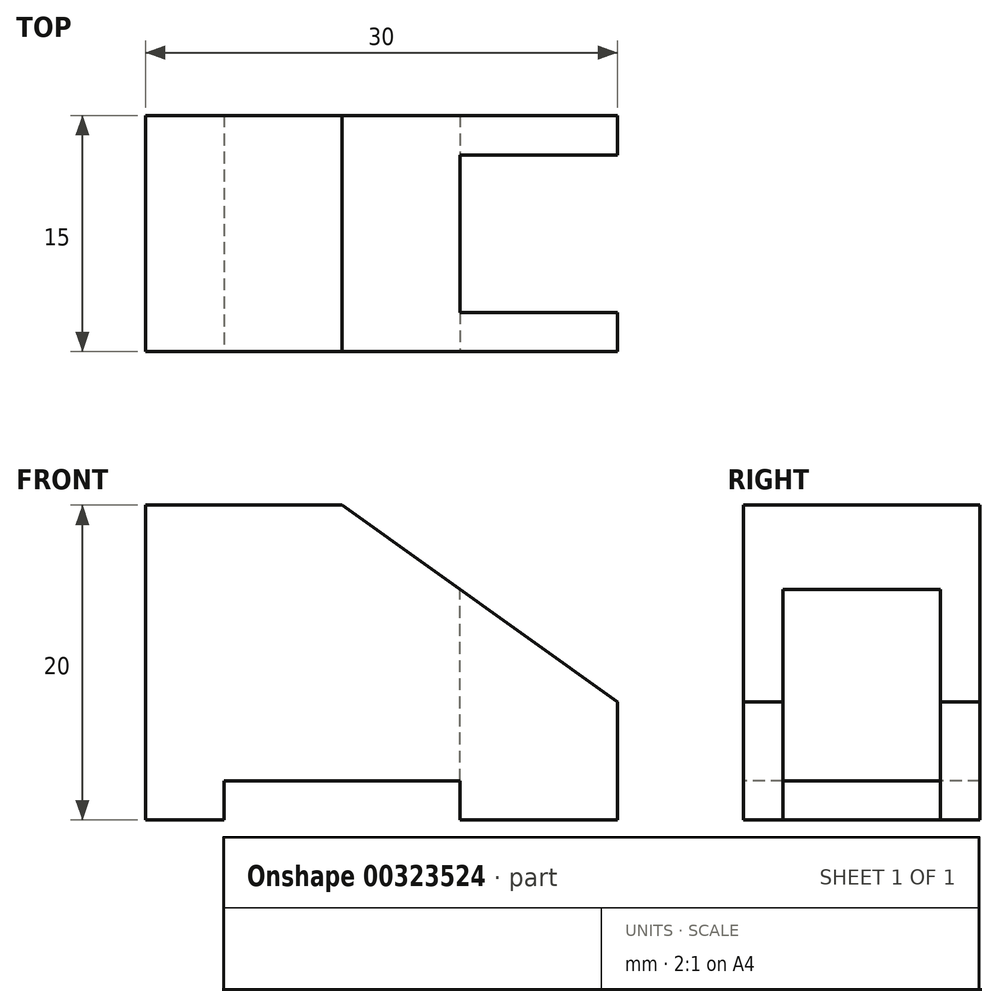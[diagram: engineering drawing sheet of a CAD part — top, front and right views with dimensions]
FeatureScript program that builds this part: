
annotation { "Feature Type Name" : "Feature", "Feature Type Description" : "" }
export const myFeature = defineFeature(function(context is Context, id is Id, definition is map)
    precondition{}
    {
        {
            var Q0;
            Q0=qCreatedBy(makeId("Front.planeOp"),FACE);
            var sketch = newSketch(context, id + "F0", { "sketchPlane" : qUnion([Q0])});
            skLineSegment(sketch, "E0", {"start": v(0, 0) * mm, "end": v(30, 0) * mm});
            skLineSegment(sketch, "E1", {"start": v(30, 0) * mm, "end": v(30, 20) * mm});
            skLineSegment(sketch, "E2", {"start": v(30, 20) * mm, "end": v(0, 20) * mm});
            skLineSegment(sketch, "E3", {"start": v(0, 20) * mm, "end": v(0, 0) * mm});
            skSolve(sketch);
        }
        {
            var Q0;
            Q0=makeQuery(id+"F0.imprint","IMPRINT",FACE,{"disambiguationData":[TD([[makeQuery(id+"F0.imprint","IMPRINT",EDGE,{"derivedFrom":sQuery(id+"F0.wireOp",EDGE,"E0")}),1.0]])]});
            extrude(context, id + "F1", {"entities" : qUnion([Q0]), "oppositeDirection" : true, "depth" : 15 * mm});
        }
        {
            var Q0;
            Q0=makeQuery(id+"F1.opExtrude","CAP_FACE",FACE,{"disambiguationData":[OSD([sQuery(id+"F0.wireOp",EDGE,"E0"),sQuery(id+"F0.wireOp",EDGE,"E1"),sQuery(id+"F0.wireOp",EDGE,"E2"),sQuery(id+"F0.wireOp",EDGE,"E3")])],"isStart":true});
            var sketch = newSketch(context, id + "F2", { "sketchPlane" : qUnion([Q0])});
            skLineSegment(sketch, "E4", {"start": v(0, 0) * mm, "end": v(5, 0) * mm, "construction": true});
            skLineSegment(sketch, "E5", {"start": v(5, 0) * mm, "end": v(5, 2.5) * mm});
            skLineSegment(sketch, "E6", {"start": v(5, 2.5) * mm, "end": v(20, 2.5) * mm});
            skLineSegment(sketch, "E7", {"start": v(20, 2.5) * mm, "end": v(20, 0) * mm});
            skLineSegment(sketch, "E8", {"start": v(20, 0) * mm, "end": v(5, 0) * mm});
            skSolve(sketch);
        }
        {
            var Q0;
            Q0=makeQuery(id+"F2.imprint","IMPRINT",FACE,{"disambiguationData":[TD([[makeQuery(id+"F2.imprint","IMPRINT",EDGE,{"derivedFrom":sQuery(id+"F2.wireOp",EDGE,"E5")}),-1.0]])]});
            extrude(context, id + "F3", {"entities" : qUnion([Q0]), "operationType" : NewBodyOperationType.REMOVE, "oppositeDirection" : true, "depth" : 25 * mm});
        }
        {
            var Q0;
            Q0=makeQuery(id+"F1.opExtrude","SWEPT_FACE",FACE,{"disambiguationData":[OSD([sQuery(id+"F0.wireOp",EDGE,"E2")])]});
            var sketch = newSketch(context, id + "F4", { "sketchPlane" : qUnion([Q0])});
            skLineSegment(sketch, "E9", {"start": v(30, 15) * mm, "end": v(30, 12.5) * mm, "construction": true});
            skLineSegment(sketch, "E10", {"start": v(30, 12.5) * mm, "end": v(20, 12.5) * mm});
            skLineSegment(sketch, "E11", {"start": v(20, 12.5) * mm, "end": v(20, 2.5) * mm});
            skLineSegment(sketch, "E12", {"start": v(20, 2.5) * mm, "end": v(30, 2.5) * mm});
            skLineSegment(sketch, "E13", {"start": v(30, 2.5) * mm, "end": v(30, 12.5) * mm});
            skSolve(sketch);
        }
        {
            var Q0;
            Q0=makeQuery(id+"F4.imprint","IMPRINT",FACE,{"disambiguationData":[TD([[makeQuery(id+"F4.imprint","IMPRINT",EDGE,{"derivedFrom":sQuery(id+"F4.wireOp",EDGE,"E10")}),1.0]])]});
            extrude(context, id + "F5", {"entities" : qUnion([Q0]), "operationType" : NewBodyOperationType.REMOVE, "oppositeDirection" : true, "depth" : 25 * mm});
        }
        {
            var Q0;
            Q0=makeQuery(id+"F1.opExtrude","CAP_FACE",FACE,{"disambiguationData":[OSD([sQuery(id+"F0.wireOp",EDGE,"E0"),sQuery(id+"F0.wireOp",EDGE,"E1"),sQuery(id+"F0.wireOp",EDGE,"E2"),sQuery(id+"F0.wireOp",EDGE,"E3")])],"isStart":true});
            var sketch = newSketch(context, id + "F6", { "sketchPlane" : qUnion([Q0])});
            skLineSegment(sketch, "E14", {"start": v(0, 20) * mm, "end": v(12.5, 20) * mm, "construction": true});
            skLineSegment(sketch, "E15", {"start": v(12.5, 20) * mm, "end": v(30, 20) * mm});
            skLineSegment(sketch, "E16", {"start": v(30, 20) * mm, "end": v(30, 7.5) * mm});
            skLineSegment(sketch, "E17", {"start": v(30, 7.5) * mm, "end": v(12.5, 20) * mm});
            skSolve(sketch);
        }
        {
            var Q0;
            Q0=makeQuery(id+"F6.imprint","IMPRINT",FACE,{"disambiguationData":[TD([[makeQuery(id+"F6.imprint","IMPRINT",EDGE,{"derivedFrom":sQuery(id+"F6.wireOp",EDGE,"E15")}),1.0]])]});
            extrude(context, id + "F7", {"entities" : qUnion([Q0]), "operationType" : NewBodyOperationType.REMOVE, "oppositeDirection" : true, "depth" : 25 * mm});
        }
    });
